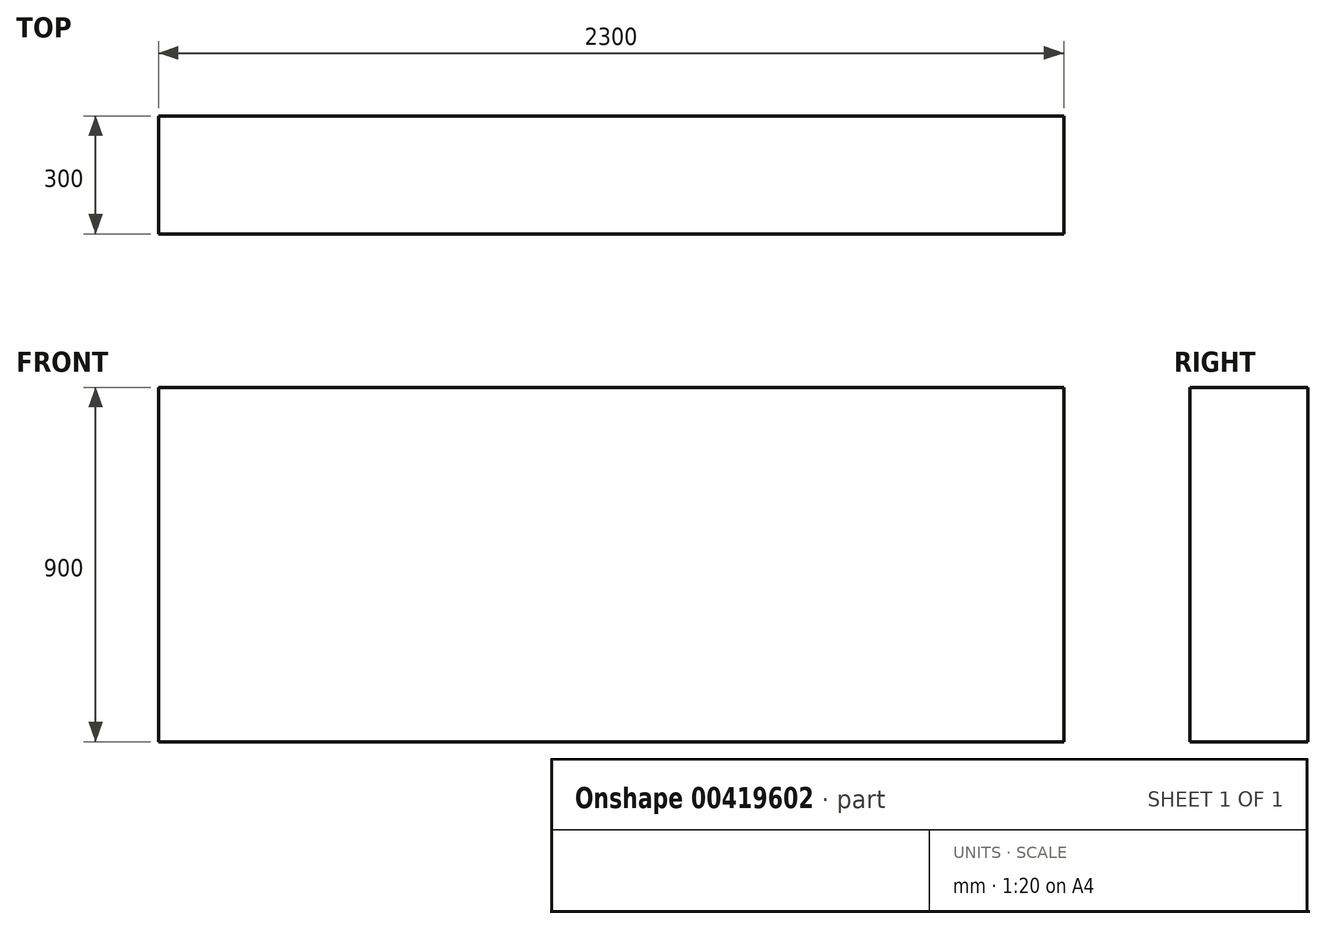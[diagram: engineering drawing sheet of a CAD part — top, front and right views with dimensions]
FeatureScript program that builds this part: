
annotation { "Feature Type Name" : "Feature", "Feature Type Description" : "" }
export const myFeature = defineFeature(function(context is Context, id is Id, definition is map)
    precondition{}
    {
        {
            var Q0;
            Q0=qCreatedBy(makeId("Top.planeOp"),FACE);
            var sketch = newSketch(context, id + "F0", { "sketchPlane" : qUnion([Q0])});
            skLineSegment(sketch, "E0.bottom", {"start": v(-2181.78, 252.12) * mm, "end": v(118.22, 252.12) * mm});
            skLineSegment(sketch, "E0.top", {"start": v(-2181.78, -47.88) * mm, "end": v(118.22, -47.88) * mm});
            skLineSegment(sketch, "E0.left", {"start": v(-2181.78, 252.12) * mm, "end": v(-2181.78, -47.88) * mm});
            skLineSegment(sketch, "E0.right", {"start": v(118.22, 252.12) * mm, "end": v(118.22, -47.88) * mm});
            skSolve(sketch);
        }
        {
            var Q0;
            Q0=makeQuery(id+"F0.imprint","IMPRINT",FACE,{"disambiguationData":[TD([[makeQuery(id+"F0.imprint","IMPRINT",EDGE,{"derivedFrom":sQuery(id+"F0.wireOp",EDGE,"E0.bottom")}),-1.0]])]});
            extrude(context, id + "F1", {"entities" : qUnion([Q0]), "depth" : 900 * mm});
        }
    });
